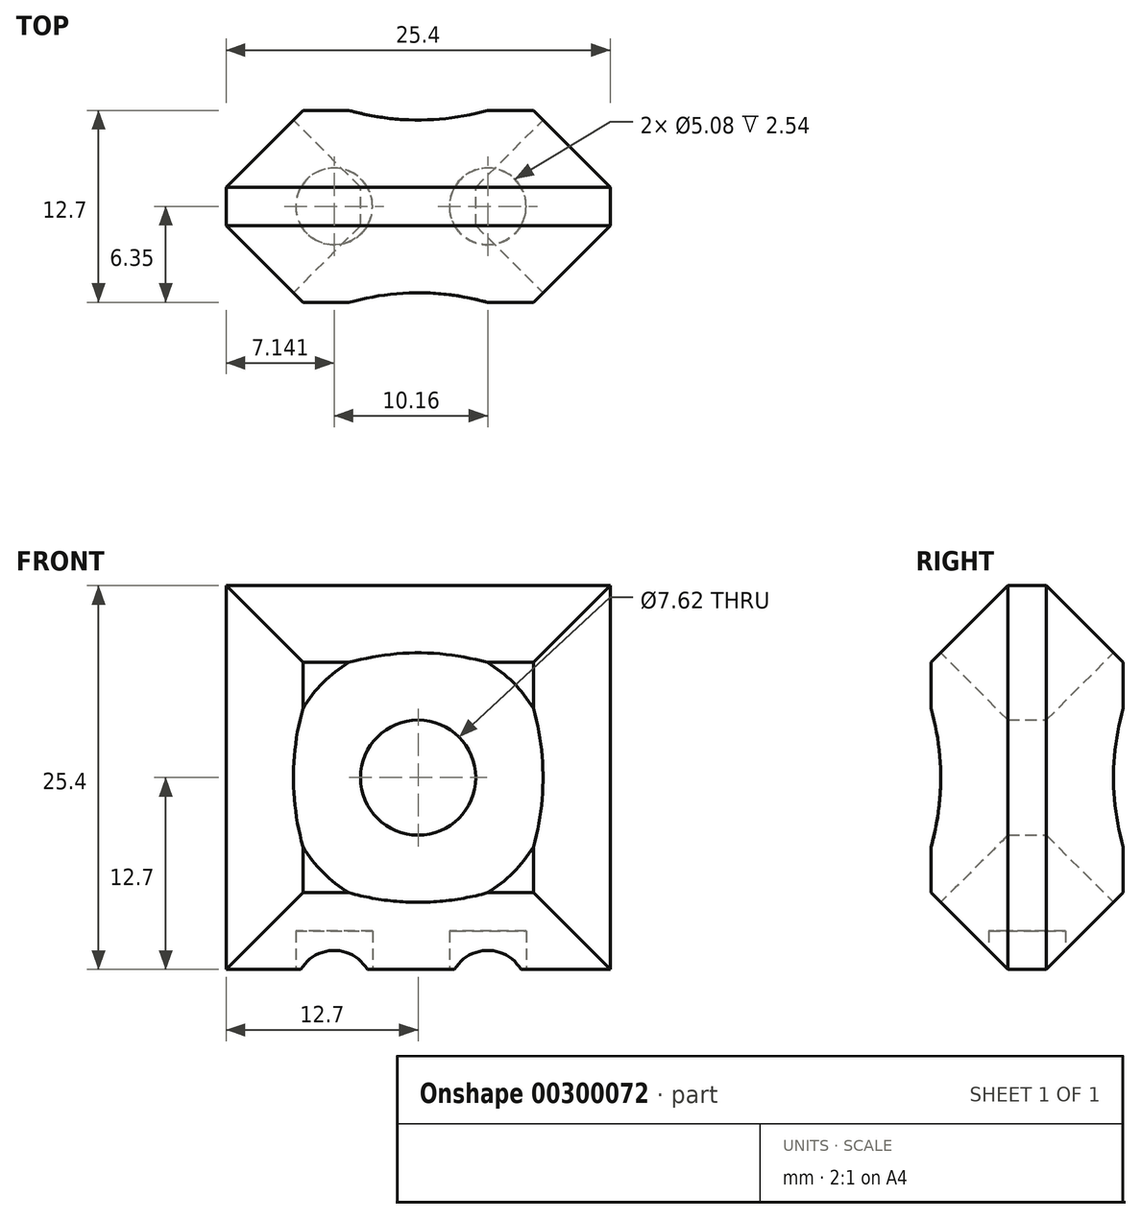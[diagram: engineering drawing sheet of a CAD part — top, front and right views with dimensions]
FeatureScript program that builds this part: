
annotation { "Feature Type Name" : "Feature", "Feature Type Description" : "" }
export const myFeature = defineFeature(function(context is Context, id is Id, definition is map)
    precondition{}
    {
        {
            var Q0;
            Q0=qCreatedBy(makeId("Front.planeOp"),FACE);
            var sketch = newSketch(context, id + "F0", { "sketchPlane" : qUnion([Q0])});
            skLineSegment(sketch, "E0.bottom", {"start": v(0, 0) * mm, "end": v(25.4, 0) * mm});
            skLineSegment(sketch, "E0.top", {"start": v(0, 25.4) * mm, "end": v(25.4, 25.4) * mm});
            skLineSegment(sketch, "E0.left", {"start": v(0, 0) * mm, "end": v(0, 25.4) * mm});
            skLineSegment(sketch, "E0.right", {"start": v(25.4, 0) * mm, "end": v(25.4, 25.4) * mm});
            skCircle(sketch, "E1", {"center": v(12.7, 12.7) * mm, "radius": 3.81 * mm});
            skLineSegment(sketch, "E2", {"start": v(12.7, 25.4) * mm, "end": v(12.7, 0) * mm});
            skLineSegment(sketch, "E3", {"start": v(0, 12.7) * mm, "end": v(25.4, 12.7) * mm});
            skSolve(sketch);
        }
        {
            var Q0;
            {var subQ5=sQuery(id+"F0.wireOp",EDGE,"E0.left");var subQ6=sQuery(id+"F0.wireOp",EDGE,"E0.top");var subQ7=makeQuery(id+"F0.imprint","INTERSECT",VERTEX,{"derivedFrom":[subQ6,subQ5]});Q0=makeQuery(id+"F0.imprint","IMPRINT",FACE,{"disambiguationData":[TD([[makeQuery(id+"F0.imprint","IMPRINT",EDGE,{"disambiguationData":[TD([[subQ7,-1.0]])],"derivedFrom":subQ6}),-1.0]])]});}
            var Q1;
            {var subQ1=sQuery(id+"F0.wireOp",EDGE,"E0.top");var subQ5=sQuery(id+"F0.wireOp",EDGE,"E0.right");var subQ6=makeQuery(id+"F0.imprint","INTERSECT",VERTEX,{"derivedFrom":[subQ1,subQ5]});Q1=makeQuery(id+"F0.imprint","IMPRINT",FACE,{"disambiguationData":[TD([[makeQuery(id+"F0.imprint","IMPRINT",EDGE,{"disambiguationData":[TD([[subQ6,1.0]])],"derivedFrom":subQ1}),-1.0]])]});}
            var Q2;
            {var subQ1=sQuery(id+"F0.wireOp",EDGE,"E0.bottom");var subQ7=sQuery(id+"F0.wireOp",EDGE,"E0.right");var subQ8=makeQuery(id+"F0.imprint","INTERSECT",VERTEX,{"derivedFrom":[subQ1,subQ7]});Q2=makeQuery(id+"F0.imprint","IMPRINT",FACE,{"disambiguationData":[TD([[makeQuery(id+"F0.imprint","IMPRINT",EDGE,{"disambiguationData":[TD([[subQ8,1.0]])],"derivedFrom":subQ1}),1.0]])]});}
            var Q3;
            {var subQ0=sQuery(id+"F0.wireOp",EDGE,"E0.left");var subQ1=sQuery(id+"F0.wireOp",EDGE,"E0.bottom");var subQ2=makeQuery(id+"F0.imprint","INTERSECT",VERTEX,{"derivedFrom":[subQ1,subQ0]});Q3=makeQuery(id+"F0.imprint","IMPRINT",FACE,{"disambiguationData":[TD([[makeQuery(id+"F0.imprint","IMPRINT",EDGE,{"disambiguationData":[TD([[subQ2,-1.0]])],"derivedFrom":subQ1}),1.0]])]});}
            extrude(context, id + "F1", {"entities" : qUnion([Q0, Q1, Q2, Q3]), "depth" : 12.7 * mm});
        }
        {
            var Q0;
            Q0=qCreatedBy(makeId("Top.planeOp"),FACE);
            var sketch = newSketch(context, id + "F2", { "sketchPlane" : qUnion([Q0])});
            skCircle(sketch, "E4", {"center": v(7.14, -6.35) * mm, "radius": 2.54 * mm});
            skCircle(sketch, "E5", {"center": v(17.3, -6.35) * mm, "radius": 2.54 * mm});
            skSolve(sketch);
        }
        {
            var Q0;
            Q0=makeQuery(id+"F2.imprint","IMPRINT",FACE,{"disambiguationData":[TD([[makeQuery(id+"F2.imprint","IMPRINT",EDGE,{"derivedFrom":sQuery(id+"F2.wireOp",EDGE,"E4")}),1.0]])]});
            var Q1;
            Q1=makeQuery(id+"F2.imprint","IMPRINT",FACE,{"disambiguationData":[TD([[makeQuery(id+"F2.imprint","IMPRINT",EDGE,{"derivedFrom":sQuery(id+"F2.wireOp",EDGE,"E5")}),1.0]])]});
            extrude(context, id + "F3", {"entities" : qUnion([Q0, Q1]), "operationType" : NewBodyOperationType.REMOVE, "depth" : 2.54 * mm});
        }
        {
            var Q0;
            Q0=makeQuery(id+"F1.opExtrude","CAP_FACE",FACE,{"disambiguationData":[OSD([sQuery(id+"F0.wireOp",EDGE,"E0.bottom"),sQuery(id+"F0.wireOp",EDGE,"E0.top"),sQuery(id+"F0.wireOp",EDGE,"E0.left"),sQuery(id+"F0.wireOp",EDGE,"E0.right"),sQuery(id+"F0.wireOp",EDGE,"E1")])],"isStart":false});
            var Q1;
            Q1=makeQuery(id+"F1.opExtrude","CAP_FACE",FACE,{"disambiguationData":[OSD([sQuery(id+"F0.wireOp",EDGE,"E0.bottom"),sQuery(id+"F0.wireOp",EDGE,"E0.top"),sQuery(id+"F0.wireOp",EDGE,"E0.left"),sQuery(id+"F0.wireOp",EDGE,"E0.right"),sQuery(id+"F0.wireOp",EDGE,"E1")])],"isStart":true});
            chamfer(context, id + "F4", {"entities" : qUnion([Q0, Q1]), "width" : 5.08 * mm, "tangentPropagation" : true});
        }
    });
